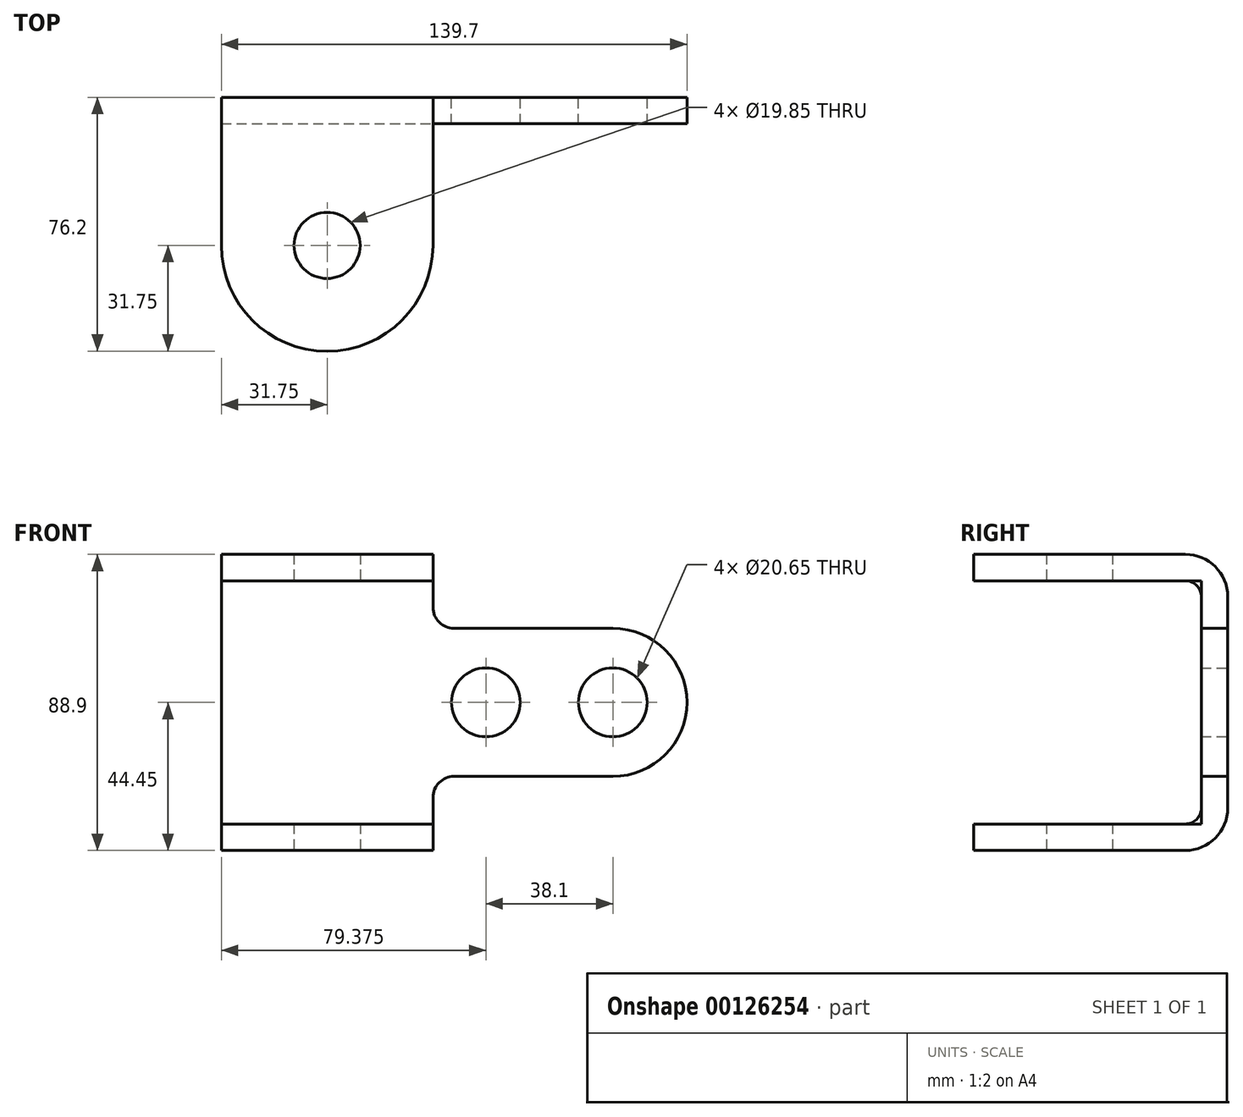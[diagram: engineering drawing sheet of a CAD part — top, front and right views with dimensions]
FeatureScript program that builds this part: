
annotation { "Feature Type Name" : "Feature", "Feature Type Description" : "" }
export const myFeature = defineFeature(function(context is Context, id is Id, definition is map)
    precondition{}
    {
        {
            var Q0;
            Q0=qCreatedBy(makeId("Front.planeOp"),FACE);
            var sketch = newSketch(context, id + "F0", { "sketchPlane" : qUnion([Q0])});
            skLineSegment(sketch, "E0", {"start": v(0, 0) * mm, "end": v(0, 88.9) * mm});
            skLineSegment(sketch, "E1", {"start": v(0, 88.9) * mm, "end": v(63.5, 88.9) * mm});
            skLineSegment(sketch, "E2", {"start": v(63.5, 88.9) * mm, "end": v(63.5, 73.02) * mm});
            skLineSegment(sketch, "E3", {"start": v(69.85, 66.67) * mm, "end": v(117.47, 66.67) * mm});
            skLineSegment(sketch, "E4", {"start": v(0, 0) * mm, "end": v(63.5, 0) * mm});
            skLineSegment(sketch, "E5", {"start": v(63.5, 0) * mm, "end": v(63.5, 15.88) * mm});
            skLineSegment(sketch, "E6", {"start": v(69.85, 22.23) * mm, "end": v(117.47, 22.23) * mm});
            skArc(sketch, "E7", {"start": v(117.47, 22.23) * mm, "mid": v(139.7, 44.45) * mm, "end": v(117.47, 66.68) * mm});
            skLineSegment(sketch, "E8", {"start": v(-74.13, 44.45) * mm, "end": v(228.96, 44.45) * mm, "construction": true});
            skPoint(sketch, "E8.endSnap0", {"position": v(139.7, 44.45) * mm});
            skPoint(sketch, "E9.visualSharp", {"position": v(63.5, 66.67) * mm});
            skArc(sketch, "E9.filletArc", {"start": v(63.5, 73.02) * mm, "mid": v(65.36, 68.53) * mm, "end": v(69.85, 66.67) * mm});
            skPoint(sketch, "E10.visualSharp", {"position": v(63.5, 22.23) * mm});
            skArc(sketch, "E10.filletArc", {"start": v(69.85, 22.23) * mm, "mid": v(65.36, 20.37) * mm, "end": v(63.5, 15.88) * mm});
            skCircle(sketch, "E11", {"center": v(117.47, 44.45) * mm, "radius": 10.33 * mm});
            skCircle(sketch, "E12", {"center": v(79.38, 44.45) * mm, "radius": 10.33 * mm});
            skSolve(sketch);
        }
        {
            var Q0;
            Q0=makeQuery(id+"F0.imprint","IMPRINT",FACE,{"disambiguationData":[TD([[makeQuery(id+"F0.imprint","IMPRINT",EDGE,{"derivedFrom":sQuery(id+"F0.wireOp",EDGE,"E0")}),-1.0]])]});
            extrude(context, id + "F1", {"entities" : qUnion([Q0]), "depth" : 7.94 * mm});
        }
        {
            var Q0;
            Q0=qCreatedBy(makeId("Top.planeOp"),FACE);
            var sketch = newSketch(context, id + "F2", { "sketchPlane" : qUnion([Q0])});
            skLineSegment(sketch, "E13.bottom", {"start": v(0, 0) * mm, "end": v(63.5, 0) * mm});
            skLineSegment(sketch, "E13.top", {"start": v(0, -44.45) * mm, "end": v(63.5, -44.45) * mm});
            skLineSegment(sketch, "E13.left", {"start": v(0, 0) * mm, "end": v(0, -44.45) * mm});
            skLineSegment(sketch, "E13.right", {"start": v(63.5, 0) * mm, "end": v(63.5, -44.45) * mm});
            skLineSegment(sketch, "E14.0", {"start": v(63.5, -7.94) * mm, "end": v(63.5, 0) * mm});
            skArc(sketch, "E15", {"start": v(0, -44.45) * mm, "mid": v(31.75, -76.2) * mm, "end": v(63.5, -44.45) * mm});
            skCircle(sketch, "E16", {"center": v(31.75, -44.45) * mm, "radius": 9.92 * mm});
            skSolve(sketch);
        }
        {
            var Q0;
            Q0=makeQuery(id+"F2.imprint","IMPRINT",FACE,{"disambiguationData":[TD([[makeQuery(id+"F2.imprint","IMPRINT",EDGE,{"derivedFrom":sQuery(id+"F2.wireOp",EDGE,"E13.bottom")}),-1.0]])]});
            var Q1;
            {var subQ0=sQuery(id+"F2.wireOp",EDGE,"E15");Q1=makeQuery(id+"F2.imprint","IMPRINT",FACE,{"disambiguationData":[TD([[makeQuery(id+"F2.imprint","IMPRINT",EDGE,{"derivedFrom":subQ0}),1.0]])]});}
            extrude(context, id + "F3", {"entities" : qUnion([Q0, Q1]), "operationType" : NewBodyOperationType.ADD, "depth" : 88.9 * mm});
        }
        {
            var Q0;
            Q0=makeQuery(id+"F3.boolean.opBoolean","MERGE",FACE,{"derivedFrom":[makeQuery(id+"F1.opExtrude","SWEPT_FACE",FACE,{"disambiguationData":[OSD([sQuery(id+"F0.wireOp",EDGE,"E2")])]}),makeQuery(id+"F1.opExtrude","SWEPT_FACE",FACE,{"disambiguationData":[OSD([sQuery(id+"F0.wireOp",EDGE,"E5")])]}),makeQuery(id+"F3.opExtrude","SWEPT_FACE",FACE,{"disambiguationData":[OSD([sQuery(id+"F2.wireOp",EDGE,"E13.right"),sQuery(id+"F2.wireOp",EDGE,"E14.0")])]})]});
            var sketch = newSketch(context, id + "F4", { "sketchPlane" : qUnion([Q0])});
            skLineSegment(sketch, "E17.bottom", {"start": v(-7.94, 7.94) * mm, "end": v(-91.56, 7.94) * mm});
            skLineSegment(sketch, "E17.top", {"start": v(-7.94, 80.96) * mm, "end": v(-91.56, 80.96) * mm});
            skLineSegment(sketch, "E17.left", {"start": v(-7.94, 7.94) * mm, "end": v(-7.94, 80.96) * mm});
            skLineSegment(sketch, "E17.right", {"start": v(-91.56, 7.94) * mm, "end": v(-91.56, 80.96) * mm});
            skSolve(sketch);
        }
        {
            var Q0;
            Q0 = qSketchRegion(id + "F4", true);
            extrude(context, id + "F5", {"entities" : qUnion([Q0]), "operationType" : NewBodyOperationType.REMOVE, "endBound" : BoundingType.THROUGH_ALL, "oppositeDirection" : true, "depth" : 25.4 * mm});
        }
        {
            var Q0;
            Q0=makeQuery(id+"F1.opExtrude","CAP_EDGE",EDGE,{"disambiguationData":[OSD([sQuery(id+"F0.wireOp",EDGE,"E1")])],"isStart":true});
            var Q1;
            Q1=makeQuery(id+"F1.opExtrude","CAP_EDGE",EDGE,{"disambiguationData":[OSD([sQuery(id+"F0.wireOp",EDGE,"E4")])],"isStart":true});
            fillet(context, id + "F6", {"entities" : qUnion([Q0, Q1]), "radius" : 12.7 * mm, "tangentPropagation" : true, "allowEdgeOverflow" : false});
        }
        {
            var Q0;
            Q0=makeQuery(id+"F1.opExtrude","SWEPT_BODY",BODY,{"disambiguationData":[OSD([sQuery(id+"F0.wireOp",EDGE,"E0"),sQuery(id+"F0.wireOp",EDGE,"E1"),sQuery(id+"F0.wireOp",EDGE,"E2"),sQuery(id+"F0.wireOp",EDGE,"E3"),sQuery(id+"F0.wireOp",EDGE,"E4"),sQuery(id+"F0.wireOp",EDGE,"E5"),sQuery(id+"F0.wireOp",EDGE,"E6"),sQuery(id+"F0.wireOp",EDGE,"E7"),sQuery(id+"F0.wireOp",EDGE,"E9.filletArc"),sQuery(id+"F0.wireOp",EDGE,"E10.filletArc"),sQuery(id+"F0.wireOp",EDGE,"E11"),sQuery(id+"F0.wireOp",EDGE,"E12")])]});
            transform(context, id + "F7", {"entities" : qUnion([Q0]), "transformType" : TransformType.TRANSLATION_3D, "dx" : 0 * mm, "dy" : 0 * mm, "dz" : 0 * mm, "makeCopy" : true});
        }
        {
            var Q0;
            Q0=makeQuery(id+"F5.boolean.opBoolean","COPY",EDGE,{"derivedFrom":makeQuery(id+"F5.opExtrude","SWEPT_EDGE",EDGE,{"disambiguationData":[OSD([sQuery(id+"F4.wireOp",EDGE,"E17.bottom"),sQuery(id+"F4.wireOp",EDGE,"E17.left")])]})});
            var Q1;
            Q1=makeQuery(id+"F5.boolean.opBoolean","COPY",EDGE,{"derivedFrom":makeQuery(id+"F5.opExtrude","SWEPT_EDGE",EDGE,{"disambiguationData":[OSD([sQuery(id+"F4.wireOp",EDGE,"E17.top"),sQuery(id+"F4.wireOp",EDGE,"E17.left")])]})});
            fillet(context, id + "F8", {"entities" : qUnion([Q0, Q1]), "radius" : 4.76 * mm, "tangentPropagation" : true, "allowEdgeOverflow" : false});
        }
    });
